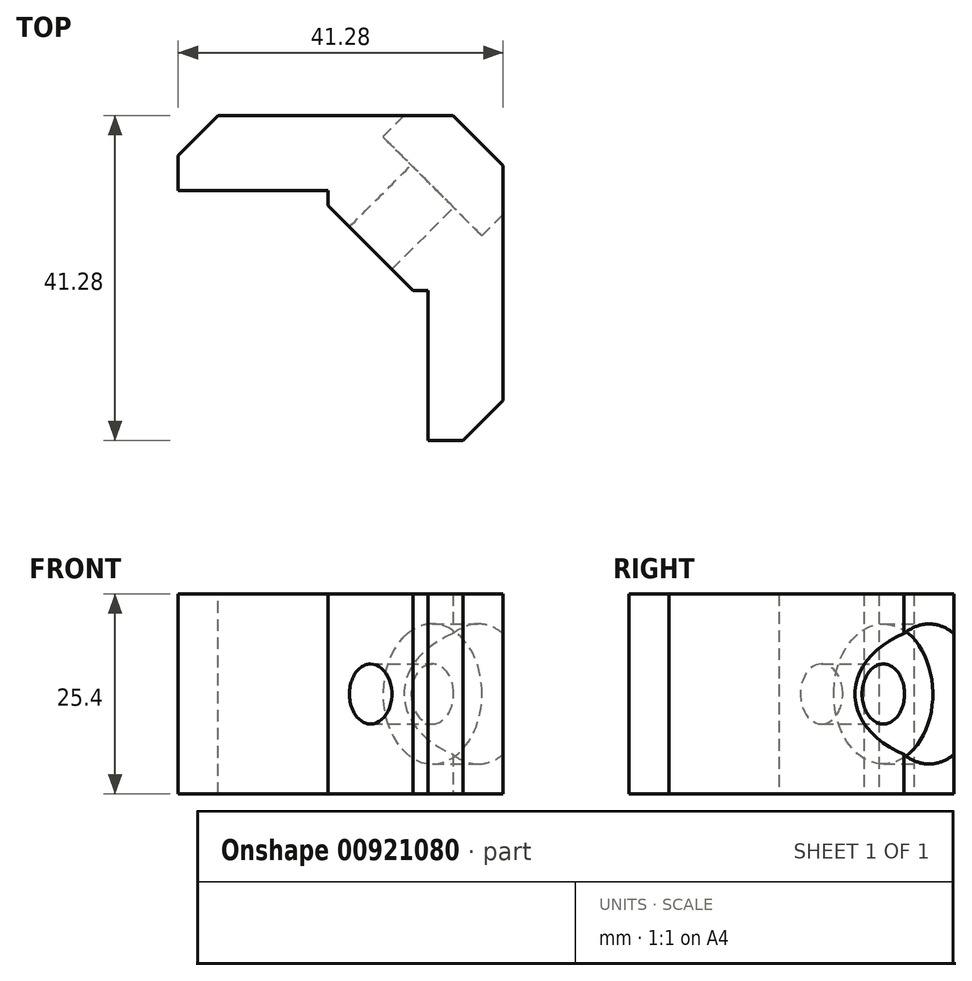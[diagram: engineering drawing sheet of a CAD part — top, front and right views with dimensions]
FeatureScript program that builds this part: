
annotation { "Feature Type Name" : "Feature", "Feature Type Description" : "" }
export const myFeature = defineFeature(function(context is Context, id is Id, definition is map)
    precondition{}
    {
        {
            var Q0;
            Q0=qCreatedBy(makeId("Top.planeOp"),FACE);
            var sketch = newSketch(context, id + "F0", { "sketchPlane" : qUnion([Q0])});
            skLineSegment(sketch, "E0", {"start": v(-31.75, 0) * mm, "end": v(-12.7, 0) * mm});
            skLineSegment(sketch, "E1", {"start": v(-12.7, 0) * mm, "end": v(-12.7, -1.9) * mm});
            skLineSegment(sketch, "E2", {"start": v(-12.7, -1.9) * mm, "end": v(-1.9, -12.7) * mm});
            skLineSegment(sketch, "E3", {"start": v(-1.9, -12.7) * mm, "end": v(0, -12.7) * mm});
            skLineSegment(sketch, "E4", {"start": v(0, -12.7) * mm, "end": v(0, -31.75) * mm});
            skLineSegment(sketch, "E5", {"start": v(0, -31.75) * mm, "end": v(9.52, -31.75) * mm});
            skLineSegment(sketch, "E6", {"start": v(9.52, -31.75) * mm, "end": v(9.52, 9.53) * mm});
            skLineSegment(sketch, "E7", {"start": v(9.52, 9.53) * mm, "end": v(-31.75, 9.53) * mm});
            skLineSegment(sketch, "E8", {"start": v(-31.75, 0) * mm, "end": v(-31.75, 9.53) * mm});
            skSolve(sketch);
        }
        {
            var Q0;
            Q0 = qSketchRegion(id + "F0", true);
            extrude(context, id + "F1", {"entities" : qUnion([Q0]), "endBound" : BoundingType.SYMMETRIC, "depth" : 25.4 * mm, "offsetDistance" : 25.4 * mm});
        }
        {
            var Q0;
            Q0=makeQuery(id+"F1.opExtrude","SWEPT_EDGE",EDGE,{"disambiguationData":[OSD([sQuery(id+"F0.wireOp",EDGE,"E6"),sQuery(id+"F0.wireOp",EDGE,"E7")])]});
            var Q1;
            Q1=qCreatedBy(makeId("Right.planeOp"),FACE);
            cPlane(context, id + "F2", {"entities" : qUnion([Q0, Q1]), "cplaneType" : CPlaneType.LINE_ANGLE, "offset" : 25.4 * mm, "angle" : 45 * degree, "oppositeDirection" : true, "width" : 152.4 * mm, "height" : 152.4 * mm});
        }
        {
            var Q0;
            Q0=qCreatedBy(id+"F2.planeOp",FACE);
            var sketch = newSketch(context, id + "F3", { "sketchPlane" : qUnion([Q0])});
            skCircle(sketch, "E9", {"center": v(0, 0) * mm, "radius": 3.81 * mm});
            skSolve(sketch);
        }
        {
            var Q0;
            Q0=makeQuery(id+"F1.opExtrude","SWEPT_EDGE",EDGE,{"disambiguationData":[OSD([sQuery(id+"F0.wireOp",EDGE,"E6"),sQuery(id+"F0.wireOp",EDGE,"E7")])]});
            chamfer(context, id + "F4", {"entities" : qUnion([Q0]), "width" : 6.35 * mm, "tangentPropagation" : true});
        }
        {
            var Q0;
            Q0 = qSketchRegion(id + "F3", true);
            extrude(context, id + "F5", {"entities" : qUnion([Q0]), "operationType" : NewBodyOperationType.REMOVE, "endBound" : BoundingType.THROUGH_ALL, "depth" : 25.4 * mm, "offsetDistance" : 25.4 * mm});
        }
        {
            var Q0;
            Q0=qCreatedBy(id+"F2.planeOp",FACE);
            var sketch = newSketch(context, id + "F6", { "sketchPlane" : qUnion([Q0])});
            skCircle(sketch, "E10", {"center": v(0, 0) * mm, "radius": 8.9 * mm});
            skSolve(sketch);
        }
        {
            var Q0;
            Q0 = qSketchRegion(id + "F6", true);
            extrude(context, id + "F7", {"entities" : qUnion([Q0]), "operationType" : NewBodyOperationType.REMOVE, "depth" : 12.7 * mm, "offsetDistance" : 25.4 * mm});
        }
        {
            var Q0;
            Q0=makeQuery(id+"F1.opExtrude","SWEPT_EDGE",EDGE,{"disambiguationData":[OSD([sQuery(id+"F0.wireOp",EDGE,"E5"),sQuery(id+"F0.wireOp",EDGE,"E6")])]});
            var Q1;
            Q1=makeQuery(id+"F1.opExtrude","SWEPT_EDGE",EDGE,{"disambiguationData":[OSD([sQuery(id+"F0.wireOp",EDGE,"E7"),sQuery(id+"F0.wireOp",EDGE,"E8")])]});
            chamfer(context, id + "F8", {"entities" : qUnion([Q0, Q1]), "width" : 5.08 * mm, "tangentPropagation" : true});
        }
    });
